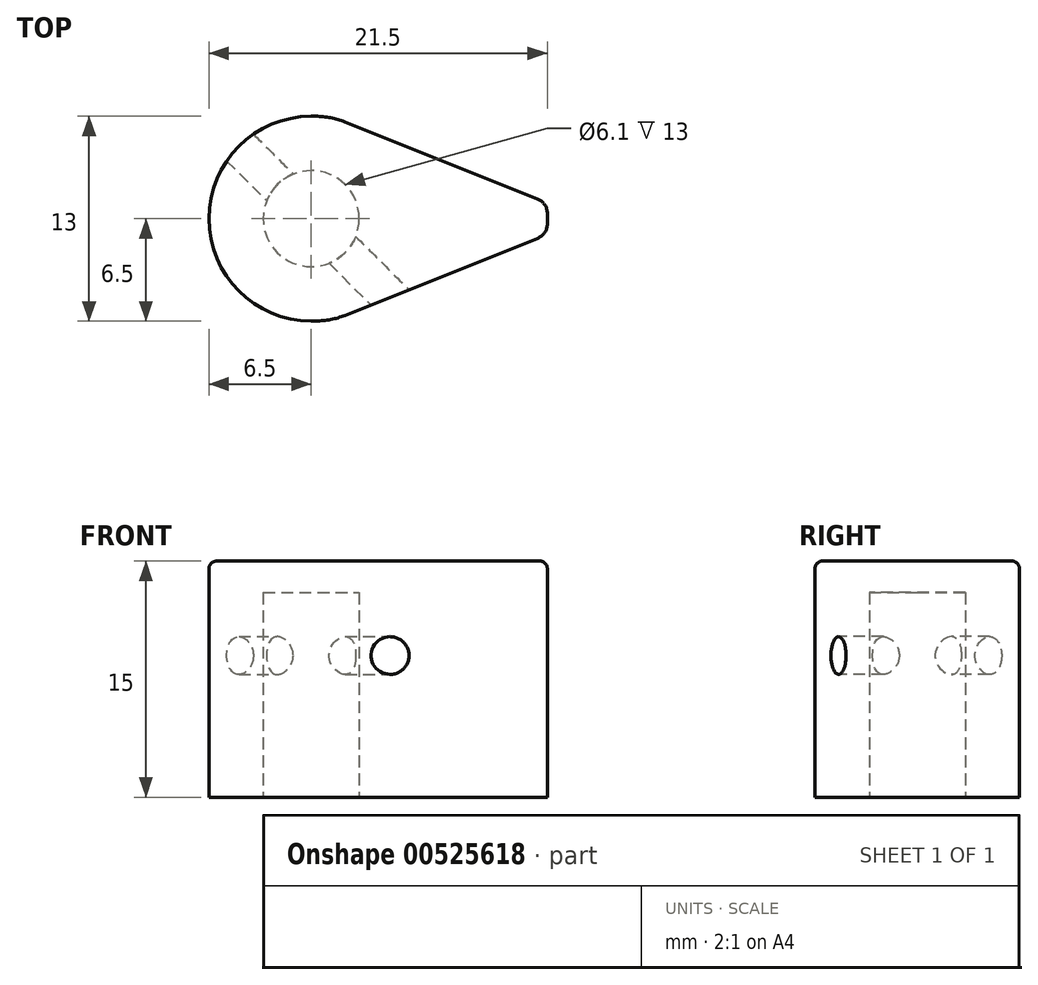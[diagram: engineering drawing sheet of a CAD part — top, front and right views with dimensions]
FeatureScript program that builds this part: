
annotation { "Feature Type Name" : "Feature", "Feature Type Description" : "" }
export const myFeature = defineFeature(function(context is Context, id is Id, definition is map)
    precondition{}
    {
        {
            var Q0;
            Q0=qCreatedBy(makeId("Front.planeOp"),FACE);
            var sketch = newSketch(context, id + "F0", { "sketchPlane" : qUnion([Q0])});
            skLineSegment(sketch, "E0", {"start": v(0, -2.23) * mm, "end": v(0, -5.1) * mm, "construction": true});
            skLineSegment(sketch, "E1", {"start": v(0, 0) * mm, "end": v(-5, 0) * mm});
            skLineSegment(sketch, "E2", {"start": v(-5, 0) * mm, "end": v(-5, 0) * mm});
            skLineSegment(sketch, "E3", {"start": v(-5, 0) * mm, "end": v(-6.5, 0) * mm});
            skLineSegment(sketch, "E4", {"start": v(-6.5, 0) * mm, "end": v(-6.5, 15) * mm});
            skLineSegment(sketch, "E5", {"start": v(-6.5, 15) * mm, "end": v(0, 15) * mm});
            skLineSegment(sketch, "E6", {"start": v(0, 0) * mm, "end": v(0, 15) * mm});
            skSolve(sketch);
        }
        {
            var Q0;
            Q0=qSketchRegion(id+"F0",true);
            var Q1;
            Q1=sQuery(id+"F0.wireOp",EDGE,"E0");
            revolve(context, id + "F1", {"entities" : qUnion([Q0]), "axis" : qUnion([Q1]), "revolveType" : RevolveType.FULL});
        }
        {
            var Q0;
            Q0=qCreatedBy(makeId("Top.planeOp"),FACE);
            var sketch = newSketch(context, id + "F2", { "sketchPlane" : qUnion([Q0])});
            skArc(sketch, "E7", {"start": v(0, 6.5) * mm, "mid": v(-6.5, 0) * mm, "end": v(0, -6.5) * mm});
            skLineSegment(sketch, "E8", {"start": v(0, 6.5) * mm, "end": v(0, -6.5) * mm});
            skLineSegment(sketch, "E9", {"start": v(0, 6.5) * mm, "end": v(1.25, 6.5) * mm});
            skLineSegment(sketch, "E10", {"start": v(1.25, 6.5) * mm, "end": v(1.25, -6.5) * mm});
            skLineSegment(sketch, "E11", {"start": v(1.25, -6.5) * mm, "end": v(0, -6.5) * mm});
            skLineSegment(sketch, "E12", {"start": v(1.25, 6.5) * mm, "end": v(15, 1) * mm});
            skLineSegment(sketch, "E13", {"start": v(15, 1) * mm, "end": v(15, -1) * mm});
            skLineSegment(sketch, "E14", {"start": v(1.25, -6.5) * mm, "end": v(15, -1) * mm});
            skPoint(sketch, "E15.orphan", {"position": v(17.5, 0) * mm});
            skSolve(sketch);
        }
        {
            var Q0;
            Q0 = qSketchRegion(id + "F2", true);
            extrude(context, id + "F3", {"entities" : qUnion([Q0]), "operationType" : NewBodyOperationType.ADD, "depth" : 15 * mm, "offsetDistance" : 25 * mm});
        }
        {
            var Q0;
            Q0=makeQuery(id+"F3.opExtrude","SWEPT_EDGE",EDGE,{"disambiguationData":[OSD([sQuery(id+"F2.wireOp",EDGE,"E9"),sQuery(id+"F2.wireOp",EDGE,"E10"),sQuery(id+"F2.wireOp",EDGE,"wZW1afJC-TMqg-X4tb-6kbN-7qLmtwS7zu3r")])]});
            var Q1;
            Q1=makeQuery(id+"F3.opExtrude","SWEPT_EDGE",EDGE,{"disambiguationData":[OSD([sQuery(id+"F2.wireOp",EDGE,"E10"),sQuery(id+"F2.wireOp",EDGE,"E11"),sQuery(id+"F2.wireOp",EDGE,"w3FL1Zt9-KYpE-BXE9-avMy-vVAwkW5g5t5w")])]});
            fillet(context, id + "F4", {"entities" : qUnion([Q0, Q1]), "radius" : 5 * mm, "tangentPropagation" : true, "allowEdgeOverflow" : false});
        }
        {
            var Q0;
            Q0=makeQuery(id+"F3.opExtrude","SWEPT_EDGE",EDGE,{"disambiguationData":[OSD([sQuery(id+"F2.wireOp",EDGE,"E12"),sQuery(id+"F2.wireOp",EDGE,"E13")])]});
            var Q1;
            Q1=makeQuery(id+"F3.opExtrude","SWEPT_EDGE",EDGE,{"disambiguationData":[OSD([sQuery(id+"F2.wireOp",EDGE,"E13"),sQuery(id+"F2.wireOp",EDGE,"E14")])]});
            fillet(context, id + "F5", {"entities" : qUnion([Q0, Q1]), "radius" : 1 * mm, "tangentPropagation" : true, "allowEdgeOverflow" : false});
        }
        {
            var Q0;
            Q0=makeQuery(id+"F3.boolean.opBoolean","MERGE",FACE,{"derivedFrom":[makeQuery(id+"F1.opRevolve","SWEPT_FACE",FACE,{"disambiguationData":[OSD([sQuery(id+"F0.wireOp",EDGE,"E1"),sQuery(id+"F0.wireOp",EDGE,"E3")])]}),makeQuery(id+"F3.opExtrude","CAP_FACE",FACE,{"disambiguationData":[OSD([sQuery(id+"F2.wireOp",EDGE,"E7"),sQuery(id+"F2.wireOp",EDGE,"E9"),sQuery(id+"F2.wireOp",EDGE,"E11"),sQuery(id+"F2.wireOp",EDGE,"E12"),sQuery(id+"F2.wireOp",EDGE,"E13"),sQuery(id+"F2.wireOp",EDGE,"E14")])],"isStart":true})]});
            var sketch = newSketch(context, id + "F6", { "sketchPlane" : qUnion([Q0])});
            skCircle(sketch, "E16", {"center": v(0, 0) * mm, "radius": 3.05 * mm});
            skSolve(sketch);
        }
        {
            var Q0;
            Q0 = qSketchRegion(id + "F6", true);
            extrude(context, id + "F7", {"entities" : qUnion([Q0]), "operationType" : NewBodyOperationType.REMOVE, "oppositeDirection" : true, "depth" : 13 * mm, "offsetDistance" : 25 * mm});
        }
        {
            var Q0;
            Q0=makeQuery(id+"F3.boolean.opBoolean","MERGE",FACE,{"derivedFrom":[makeQuery(id+"F1.opRevolve","SWEPT_FACE",FACE,{"disambiguationData":[OSD([sQuery(id+"F0.wireOp",EDGE,"E5")])]}),makeQuery(id+"F3.opExtrude","CAP_FACE",FACE,{"disambiguationData":[OSD([sQuery(id+"F2.wireOp",EDGE,"E7"),sQuery(id+"F2.wireOp",EDGE,"E9"),sQuery(id+"F2.wireOp",EDGE,"E11"),sQuery(id+"F2.wireOp",EDGE,"E12"),sQuery(id+"F2.wireOp",EDGE,"E13"),sQuery(id+"F2.wireOp",EDGE,"E14")])],"isStart":false})]});
            fillet(context, id + "F8", {"entities" : qUnion([Q0]), "radius" : 0.5 * mm, "tangentPropagation" : true, "allowEdgeOverflow" : false});
        }
        {
            var Q0;
            Q0=sQuery(id+"F0.wireOp",EDGE,"E6");
            cPlane(context, id + "F9", {"entities" : qUnion([Q0]), "cplaneType" : CPlaneType.LINE_ANGLE, "offset" : 25 * mm, "angle" : 135 * degree, "width" : 150 * mm, "height" : 150 * mm});
        }
        {
            var Q0;
            Q0=qCreatedBy(id+"F9.planeOp",FACE);
            var sketch = newSketch(context, id + "F10", { "sketchPlane" : qUnion([Q0])});
            skCircle(sketch, "E17", {"center": v(0, 9) * mm, "radius": 1.2 * mm});
            skSolve(sketch);
        }
        {
            var Q0;
            Q0 = qSketchRegion(id + "F10", true);
            extrude(context, id + "F11", {"entities" : qUnion([Q0]), "operationType" : NewBodyOperationType.REMOVE, "endBound" : BoundingType.SYMMETRIC, "depth" : 25 * mm, "offsetDistance" : 25 * mm});
        }
    });
